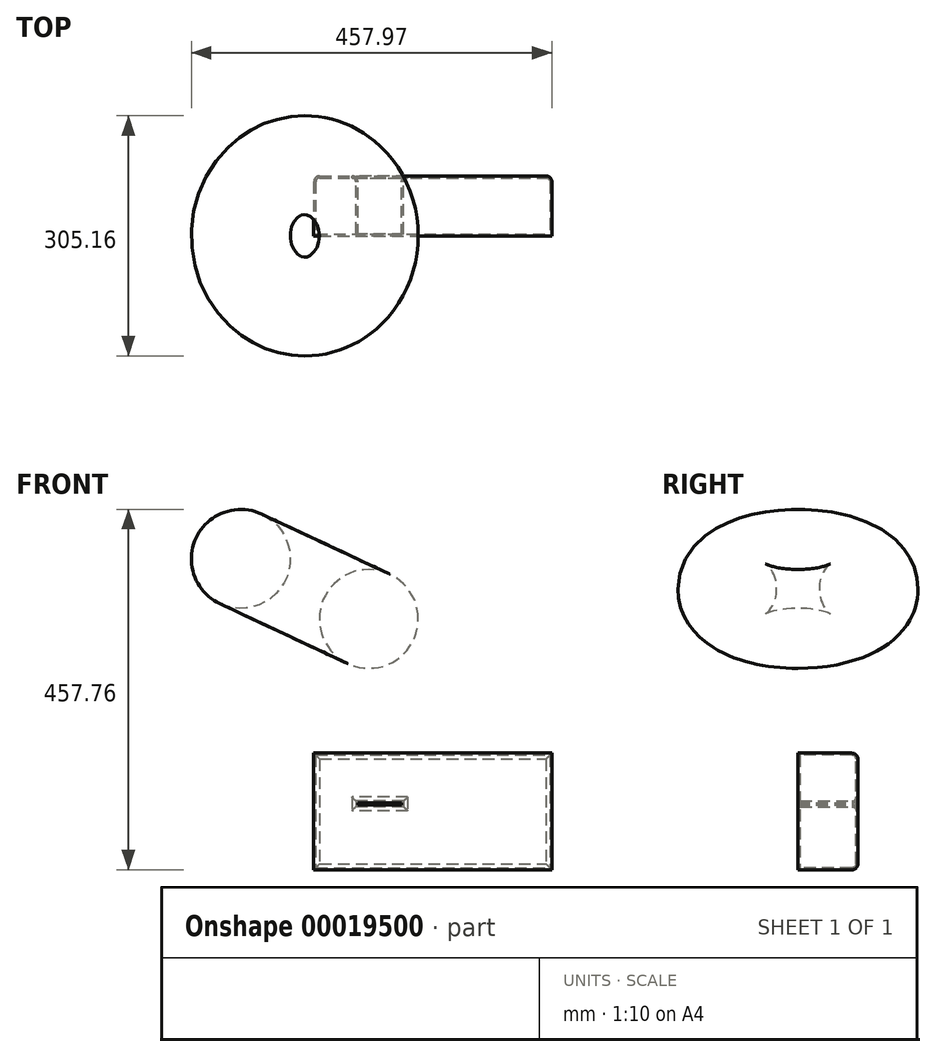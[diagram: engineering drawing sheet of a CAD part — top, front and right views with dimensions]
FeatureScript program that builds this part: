
annotation { "Feature Type Name" : "Feature", "Feature Type Description" : "" }
export const myFeature = defineFeature(function(context is Context, id is Id, definition is map)
    precondition{}
    {
        {
            var Q0;
            Q0=qCreatedBy(makeId("Front.planeOp"),FACE);
            var sketch = newSketch(context, id + "F0", { "sketchPlane" : qUnion([Q0])});
            skLineSegment(sketch, "E0.bottom", {"start": v(-267.06, 67.48) * mm, "end": v(35.4, 67.48) * mm});
            skLineSegment(sketch, "E0.top", {"start": v(-267.06, -80.7) * mm, "end": v(35.4, -80.7) * mm});
            skLineSegment(sketch, "E0.left", {"start": v(-267.06, 67.48) * mm, "end": v(-267.06, -80.7) * mm});
            skLineSegment(sketch, "E0.right", {"start": v(35.4, 67.48) * mm, "end": v(35.4, -80.7) * mm});
            skSolve(sketch);
        }
        {
            var Q0;
            Q0=makeQuery(id+"F0.imprint","IMPRINT",FACE,{"disambiguationData":[TD([[makeQuery(id+"F0.imprint","IMPRINT",EDGE,{"derivedFrom":sQuery(id+"F0.wireOp",EDGE,"E0.bottom")}),-1.0]])]});
            extrude(context, id + "F1", {"entities" : qUnion([Q0]), "oppositeDirection" : true, "depth" : 76.2 * mm});
        }
        {
            var Q0;
            Q0=makeQuery(id+"F1.opExtrude","CAP_FACE",FACE,{"disambiguationData":[OSD([sQuery(id+"F0.wireOp",EDGE,"E0.bottom"),sQuery(id+"F0.wireOp",EDGE,"E0.top"),sQuery(id+"F0.wireOp",EDGE,"E0.left"),sQuery(id+"F0.wireOp",EDGE,"E0.right")])],"isStart":false});
            var sketch = newSketch(context, id + "F2", { "sketchPlane" : qUnion([Q0])});
            skLineSegment(sketch, "E1.bottom", {"start": v(155.47, 3.98) * mm, "end": v(211.1, 3.98) * mm});
            skLineSegment(sketch, "E1.top", {"start": v(155.47, 1.97) * mm, "end": v(211.1, 1.97) * mm});
            skLineSegment(sketch, "E1.left", {"start": v(155.47, 3.98) * mm, "end": v(155.47, 1.97) * mm});
            skLineSegment(sketch, "E1.right", {"start": v(211.1, 3.98) * mm, "end": v(211.1, 1.97) * mm});
            skSolve(sketch);
        }
        {
            var Q0;
            Q0=makeQuery(id+"F2.imprint","IMPRINT",FACE,{"disambiguationData":[TD([[makeQuery(id+"F2.imprint","IMPRINT",EDGE,{"derivedFrom":sQuery(id+"F2.wireOp",EDGE,"E1.bottom")}),-1.0]])]});
            extrude(context, id + "F3", {"entities" : qUnion([Q0]), "operationType" : NewBodyOperationType.REMOVE, "oppositeDirection" : true, "depth" : 76.2 * mm});
        }
        {
            var Q0;
            Q0=qCreatedBy(makeId("Front.planeOp"),FACE);
            var sketch = newSketch(context, id + "F4", { "sketchPlane" : qUnion([Q0])});
            skCircle(sketch, "E2", {"center": v(-359.78, 314.3) * mm, "radius": 62.78 * mm});
            skLineSegment(sketch, "E3", {"start": v(-263.57, 307.94) * mm, "end": v(-308.43, 212.3) * mm});
            skSolve(sketch);
        }
        {
            var Q0;
            Q0=makeQuery(id+"F4.imprint","IMPRINT",FACE,{"disambiguationData":[TD([[makeQuery(id+"F4.imprint","IMPRINT",EDGE,{"derivedFrom":sQuery(id+"F4.wireOp",EDGE,"E2")}),1.0]])]});
            var Q1;
            Q1=sQuery(id+"F4.wireOp",EDGE,"E3");
            revolve(context, id + "F5", {"entities" : qUnion([Q0]), "axis" : qUnion([Q1]), "revolveType" : RevolveType.FULL});
        }
        {
            var Q0;
            Q0=makeQuery(id+"F1.opExtrude","CAP_FACE",FACE,{"disambiguationData":[OSD([sQuery(id+"F0.wireOp",EDGE,"E0.bottom"),sQuery(id+"F0.wireOp",EDGE,"E0.top"),sQuery(id+"F0.wireOp",EDGE,"E0.left"),sQuery(id+"F0.wireOp",EDGE,"E0.right")])],"isStart":false});
            var Q1;
            Q1=makeQuery(id+"F1.opExtrude","CAP_EDGE",EDGE,{"disambiguationData":[OSD([sQuery(id+"F0.wireOp",EDGE,"E0.left")])],"isStart":false});
            fillet(context, id + "F6", {"entities" : qUnion([Q0, Q1]), "radius" : 7.62 * mm, "tangentPropagation" : true, "allowEdgeOverflow" : false});
        }
        {
            var Q0;
            Q0=makeQuery(id+"F1.opExtrude","CAP_FACE",FACE,{"disambiguationData":[OSD([sQuery(id+"F0.wireOp",EDGE,"E0.bottom"),sQuery(id+"F0.wireOp",EDGE,"E0.top"),sQuery(id+"F0.wireOp",EDGE,"E0.left"),sQuery(id+"F0.wireOp",EDGE,"E0.right")])],"isStart":false});
            shell(context, id + "F7", {"entities" : qUnion([Q0]), "thickness" : 2.54 * mm});
        }
    });
